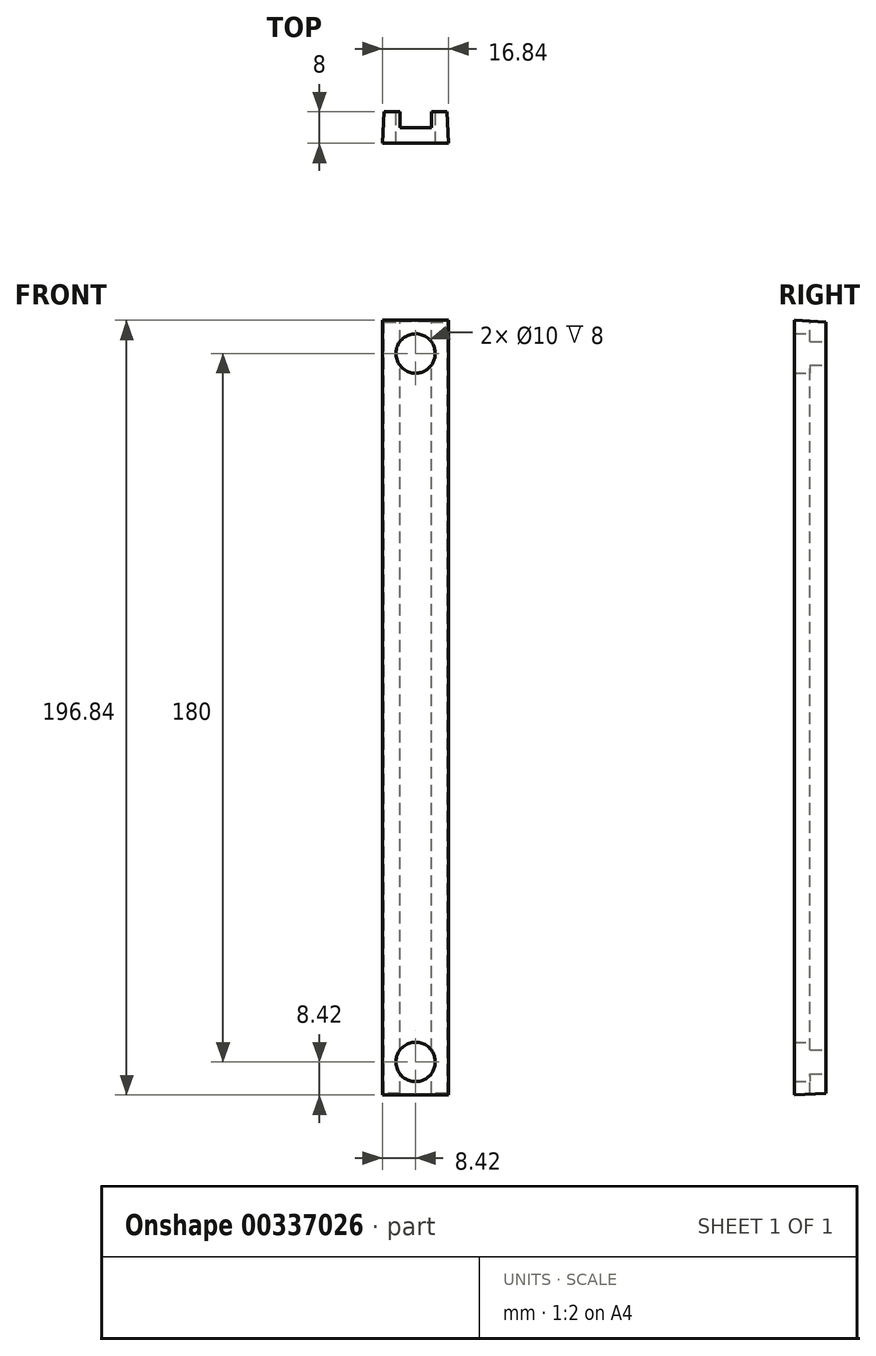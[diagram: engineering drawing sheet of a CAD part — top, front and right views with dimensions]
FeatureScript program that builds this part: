
annotation { "Feature Type Name" : "Feature", "Feature Type Description" : "" }
export const myFeature = defineFeature(function(context is Context, id is Id, definition is map)
    precondition{}
    {
        {
            var Q0;
            Q0=qCreatedBy(makeId("Front.planeOp"),FACE);
            var sketch = newSketch(context, id + "F0", { "sketchPlane" : qUnion([Q0])});
            skLineSegment(sketch, "E0.bottom", {"start": v(8, -98) * mm, "end": v(-8, -98) * mm});
            skLineSegment(sketch, "E0.top", {"start": v(8, 98) * mm, "end": v(-8, 98) * mm});
            skLineSegment(sketch, "E0.left", {"start": v(8, -98) * mm, "end": v(8, 98) * mm});
            skLineSegment(sketch, "E0.right", {"start": v(-8, -98) * mm, "end": v(-8, 98) * mm});
            skPoint(sketch, "E0.middle", {"position": v(0, 0) * mm});
            skSolve(sketch);
        }
        {
            var Q0;
            Q0=qSketchRegion(id+"F0",true);
            extrude(context, id + "F1", {"entities" : qUnion([Q0]), "depth" : 8 * mm, "hasDraft" : true, "draftAngle" : 3 * degree});
        }
        {
            var Q0;
            Q0=qSketchRegion(id+"F0",true);
            var sketch = newSketch(context, id + "F2", { "sketchPlane" : qUnion([Q0])});
            skLineSegment(sketch, "E1.bottom", {"start": v(4, -100) * mm, "end": v(-4, -100) * mm});
            skLineSegment(sketch, "E1.top", {"start": v(4, 100) * mm, "end": v(-4, 100) * mm});
            skLineSegment(sketch, "E1.left", {"start": v(4, -100) * mm, "end": v(4, 100) * mm});
            skLineSegment(sketch, "E1.right", {"start": v(-4, -100) * mm, "end": v(-4, 100) * mm});
            skPoint(sketch, "E1.middle", {"position": v(0, 0) * mm});
            skSolve(sketch);
        }
        {
            var Q0;
            Q0=qSketchRegion(id+"F2",true);
            extrude(context, id + "F3", {"entities" : qUnion([Q0]), "operationType" : NewBodyOperationType.REMOVE, "depth" : 4 * mm});
        }
        {
            var Q0;
            Q0=qCreatedBy(makeId("Front.planeOp"),FACE);
            var sketch = newSketch(context, id + "F4", { "sketchPlane" : qUnion([Q0])});
            skCircle(sketch, "E2", {"center": v(0, 90) * mm, "radius": 5 * mm});
            skCircle(sketch, "E3", {"center": v(0, -90) * mm, "radius": 5 * mm});
            skSolve(sketch);
        }
        {
            var Q0;
            Q0=qSketchRegion(id+"F4",true);
            extrude(context, id + "F5", {"entities" : qUnion([Q0]), "operationType" : NewBodyOperationType.REMOVE, "depth" : 25.4 * mm});
        }
    });
